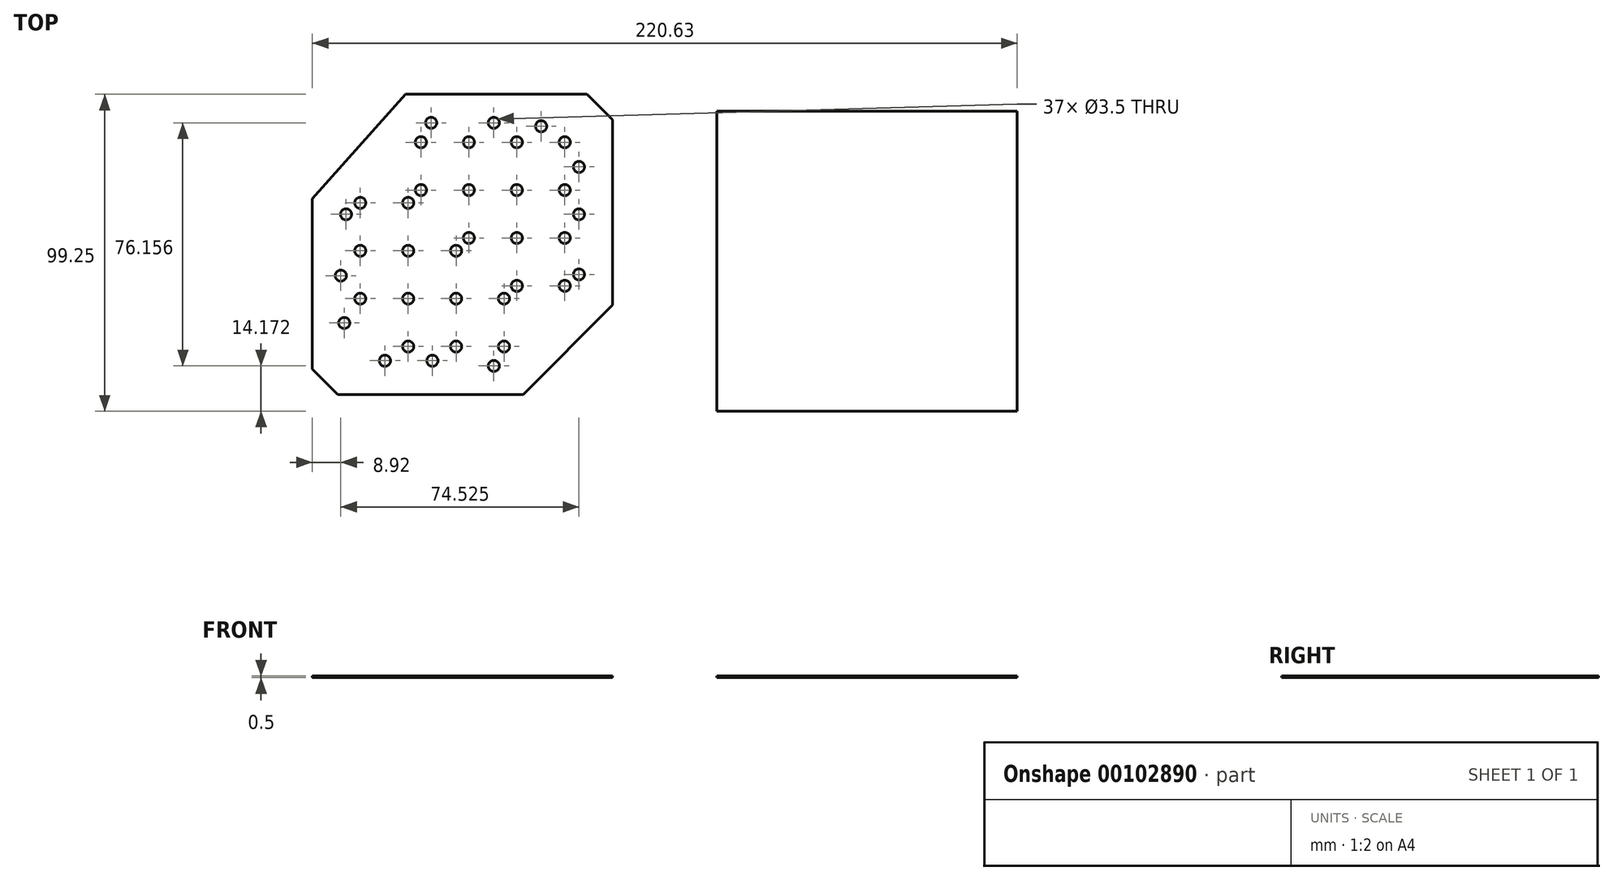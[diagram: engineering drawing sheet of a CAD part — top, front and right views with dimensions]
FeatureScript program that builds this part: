
annotation { "Feature Type Name" : "Feature", "Feature Type Description" : "" }
export const myFeature = defineFeature(function(context is Context, id is Id, definition is map)
    precondition{}
    {
        {
            var Q0;
            Q0=qCreatedBy(makeId("Top.planeOp"),FACE);
            var sketch = newSketch(context, id + "F0", { "sketchPlane" : qUnion([Q0])});
            skLineSegment(sketch, "E0.bottom", {"start": v(-128.87, 27.42) * mm, "end": v(-34.87, 27.42) * mm});
            skLineSegment(sketch, "E0.top", {"start": v(-128.87, -66.58) * mm, "end": v(-34.87, -66.58) * mm});
            skLineSegment(sketch, "E0.left", {"start": v(-128.87, 27.42) * mm, "end": v(-128.87, -66.58) * mm});
            skLineSegment(sketch, "E0.right", {"start": v(-34.87, 27.42) * mm, "end": v(-34.87, -66.58) * mm});
            skPoint(sketch, "E0.middle", {"position": v(-81.87, -19.58) * mm});
            skSolve(sketch);
        }
        {
            var Q0;
            Q0=qCreatedBy(makeId("Top.planeOp"),FACE);
            var sketch = newSketch(context, id + "F1", { "sketchPlane" : qUnion([Q0])});
            skCircle(sketch, "E1", {"center": v(-172.06, 9.94) * mm, "radius": 1.75 * mm});
            skCircle(sketch, "E2.0", {"center": v(-176.5, 17.67) * mm, "radius": 1.75 * mm});
            skCircle(sketch, "E3.0.1.0", {"center": v(-176.5, 2.67) * mm, "radius": 1.75 * mm});
            skCircle(sketch, "E3.0.2.0", {"center": v(-176.5, -12.33) * mm, "radius": 1.75 * mm});
            skCircle(sketch, "E3.0.3.0", {"center": v(-176.5, -27.33) * mm, "radius": 1.75 * mm});
            skCircle(sketch, "E3.1.0.0", {"center": v(-191.5, 17.67) * mm, "radius": 1.75 * mm});
            skCircle(sketch, "E3.1.1.0", {"center": v(-191.5, 2.67) * mm, "radius": 1.75 * mm});
            skCircle(sketch, "E3.1.2.0", {"center": v(-191.5, -12.33) * mm, "radius": 1.75 * mm});
            skCircle(sketch, "E3.1.3.0", {"center": v(-191.5, -27.33) * mm, "radius": 1.75 * mm});
            skCircle(sketch, "E3.2.0.0", {"center": v(-206.5, 17.67) * mm, "radius": 1.75 * mm});
            skCircle(sketch, "E3.2.1.0", {"center": v(-206.5, 2.67) * mm, "radius": 1.75 * mm});
            skCircle(sketch, "E3.2.2.0", {"center": v(-206.5, -12.33) * mm, "radius": 1.75 * mm});
            skCircle(sketch, "E3.3.0.0", {"center": v(-221.5, 17.67) * mm, "radius": 1.75 * mm});
            skCircle(sketch, "E3.3.1.0", {"center": v(-221.5, 2.67) * mm, "radius": 1.75 * mm});
            skLineSegment(sketch, "E3.direction1", {"start": v(-176.5, 17.67) * mm, "end": v(-191.5, 17.67) * mm, "construction": true});
            skLineSegment(sketch, "E3.direction2", {"start": v(-176.5, 17.67) * mm, "end": v(-176.5, 2.67) * mm, "construction": true});
            skCircle(sketch, "E4.MirrorC", {"center": v(-195.5, -46.33) * mm, "radius": 1.75 * mm});
            skCircle(sketch, "E5.MirrorC", {"center": v(-195.5, -31.33) * mm, "radius": 1.75 * mm});
            skCircle(sketch, "E6.MirrorC", {"center": v(-210.5, -31.33) * mm, "radius": 1.75 * mm});
            skCircle(sketch, "E7.MirrorC", {"center": v(-210.5, -16.33) * mm, "radius": 1.75 * mm});
            skCircle(sketch, "E8.MirrorC", {"center": v(-210.5, -46.33) * mm, "radius": 1.75 * mm});
            skCircle(sketch, "E9.MirrorC", {"center": v(-225.5, -31.33) * mm, "radius": 1.75 * mm});
            skCircle(sketch, "E10.MirrorC", {"center": v(-225.5, -46.33) * mm, "radius": 1.75 * mm});
            skCircle(sketch, "E11.MirrorC", {"center": v(-240.5, -31.33) * mm, "radius": 1.75 * mm});
            skCircle(sketch, "E12.MirrorC", {"center": v(-240.5, -16.33) * mm, "radius": 1.75 * mm});
            skCircle(sketch, "E13.MirrorC", {"center": v(-225.5, -16.33) * mm, "radius": 1.75 * mm});
            skCircle(sketch, "E14.MirrorC", {"center": v(-225.5, -1.33) * mm, "radius": 1.75 * mm});
            skCircle(sketch, "E15.MirrorC", {"center": v(-240.5, -1.33) * mm, "radius": 1.75 * mm});
            skCircle(sketch, "E16", {"center": v(-172.06, -4.91) * mm, "radius": 1.75 * mm});
            skLineSegment(sketch, "E17", {"start": v(-176.5, 2.67) * mm, "end": v(-191.5, 17.67) * mm, "construction": true});
            skLineSegment(sketch, "E18", {"start": v(-176.5, 17.67) * mm, "end": v(-184.28, 10.44) * mm, "construction": true});
            skCircle(sketch, "E19.MirrorC", {"center": v(-198.7, 23.75) * mm, "radius": 1.75 * mm});
            skCircle(sketch, "E20.MirrorC", {"center": v(-183.89, 22.67) * mm, "radius": 1.75 * mm});
            skCircle(sketch, "E21.MirrorC", {"center": v(-246.58, -24.13) * mm, "radius": 1.75 * mm});
            skCircle(sketch, "E22.MirrorC", {"center": v(-217.92, -50.78) * mm, "radius": 1.75 * mm});
            skCircle(sketch, "E23.MirrorC", {"center": v(-232.77, -50.78) * mm, "radius": 1.75 * mm});
            skCircle(sketch, "E24.MirrorC", {"center": v(-245.5, -38.94) * mm, "radius": 1.75 * mm});
            skLineSegment(sketch, "E25.0", {"start": v(-255.5, 24.67) * mm, "end": v(-255.5, -53.33) * mm});
            skLineSegment(sketch, "E26.0", {"start": v(-161.5, 24.67) * mm, "end": v(-161.5, -53.33) * mm});
            skLineSegment(sketch, "E27.0", {"start": v(-247.5, 32.67) * mm, "end": v(-169.5, 32.67) * mm});
            skLineSegment(sketch, "E28.0", {"start": v(-247.5, -61.33) * mm, "end": v(-169.5, -61.33) * mm});
            skLineSegment(sketch, "E29", {"start": v(-255.5, -14.33) * mm, "end": v(-161.5, -14.33) * mm, "construction": true});
            skLineSegment(sketch, "E30", {"start": v(-208.5, -61.33) * mm, "end": v(-208.5, 32.67) * mm, "construction": true});
            skCircle(sketch, "E31.MirrorC", {"center": v(-172.06, -23.75) * mm, "radius": 1.75 * mm});
            skCircle(sketch, "E32.MirrorC", {"center": v(-198.7, -52.4) * mm, "radius": 1.75 * mm});
            skCircle(sketch, "E33.MirrorC", {"center": v(-244.95, -4.91) * mm, "radius": 1.75 * mm});
            skCircle(sketch, "E34.MirrorC", {"center": v(-218.3, 23.75) * mm, "radius": 1.75 * mm});
            skLineSegment(sketch, "E35.49", {"start": v(-128.87, 27.42) * mm, "end": v(-128.87, -66.58) * mm});
            skLineSegment(sketch, "E35.50", {"start": v(-128.87, 27.42) * mm, "end": v(-34.87, 27.42) * mm});
            skLineSegment(sketch, "E35.51", {"start": v(-128.87, -66.58) * mm, "end": v(-34.87, -66.58) * mm});
            skLineSegment(sketch, "E35.52", {"start": v(-34.87, 27.42) * mm, "end": v(-34.87, -66.58) * mm});
            skLineSegment(sketch, "E36", {"start": v(-169.5, -61.33) * mm, "end": v(-161.5, -53.33) * mm});
            skLineSegment(sketch, "E37", {"start": v(-161.5, 24.67) * mm, "end": v(-169.5, 32.67) * mm});
            skLineSegment(sketch, "E38", {"start": v(-247.5, 32.67) * mm, "end": v(-255.5, 24.67) * mm});
            skLineSegment(sketch, "E39", {"start": v(-255.5, -53.33) * mm, "end": v(-247.5, -61.33) * mm});
            skLineSegment(sketch, "E40", {"start": v(-189.47, -61.33) * mm, "end": v(-161.5, -33.36) * mm});
            skLineSegment(sketch, "E41", {"start": v(-255.5, 0) * mm, "end": v(-226.35, 32.67) * mm});
            skSolve(sketch);
        }
        {
            var Q0;
            Q0 = qSketchRegion(id + "F0", true);
            extrude(context, id + "F2", {"entities" : qUnion([Q0]), "depth" : 0.5 * mm});
        }
        {
            var Q0;
            Q0 = qSketchRegion(id + "F1", true);
            var Q1;
            Q1=makeQuery(id+"F0.imprint","IMPRINT",FACE,{"disambiguationData":[TD([[makeQuery(id+"F0.imprint","IMPRINT",EDGE,{"derivedFrom":sQuery(id+"F0.wireOp",EDGE,"E0.bottom")}),-1.0]])]});
            extrude(context, id + "F3", {"entities" : qUnion([Q0, Q1]), "depth" : 0.5 * mm});
        }
        {
            var Q0;
            {var subQ0=sQuery(id+"F1.wireOp",EDGE,"E36");Q0=makeQuery(id+"F1.imprint","IMPRINT",FACE,{"disambiguationData":[TD([[makeQuery(id+"F1.imprint","IMPRINT",EDGE,{"derivedFrom":subQ0}),1.0]])]});}
            var Q1;
            {var subQ0=sQuery(id+"F1.wireOp",EDGE,"E38");Q1=makeQuery(id+"F1.imprint","IMPRINT",FACE,{"disambiguationData":[TD([[makeQuery(id+"F1.imprint","IMPRINT",EDGE,{"derivedFrom":subQ0}),1.0]])]});}
            extrude(context, id + "F4", {"entities" : qUnion([Q0, Q1]), "operationType" : NewBodyOperationType.REMOVE, "depth" : 25 * mm});
        }
    });
